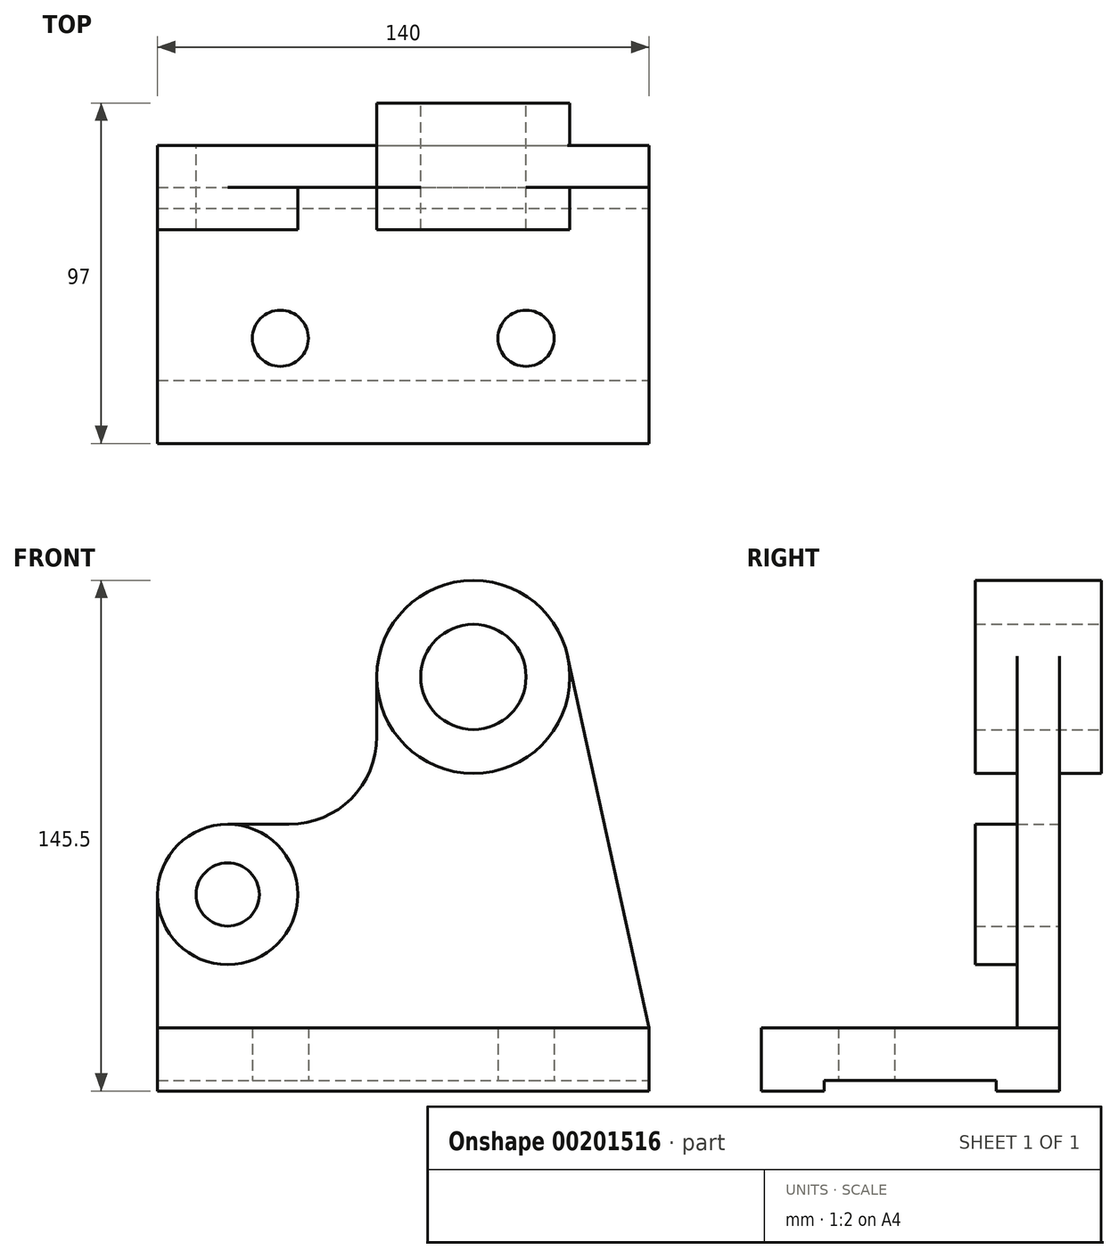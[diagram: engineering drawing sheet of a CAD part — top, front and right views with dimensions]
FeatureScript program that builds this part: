
annotation { "Feature Type Name" : "Feature", "Feature Type Description" : "" }
export const myFeature = defineFeature(function(context is Context, id is Id, definition is map)
    precondition{}
    {
        {
            var Q0;
            Q0=qCreatedBy(makeId("Front.planeOp"),FACE);
            var sketch = newSketch(context, id + "F0", { "sketchPlane" : qUnion([Q0])});
            skLineSegment(sketch, "E0.bottom", {"start": v(-70, 0) * mm, "end": v(70, 0) * mm});
            skLineSegment(sketch, "E0.top", {"start": v(-70, -18) * mm, "end": v(70, -18) * mm});
            skLineSegment(sketch, "E0.left", {"start": v(-70, 0) * mm, "end": v(-70, -18) * mm});
            skLineSegment(sketch, "E0.right", {"start": v(70, 0) * mm, "end": v(70, -18) * mm});
            skLineSegment(sketch, "E1", {"start": v(-70, 0) * mm, "end": v(-70, 38) * mm});
            skLineSegment(sketch, "E2", {"start": v(-50, 58) * mm, "end": v(-32.5, 58) * mm});
            skLineSegment(sketch, "E3", {"start": v(70, 0) * mm, "end": v(46.87, 105.87) * mm});
            skCircle(sketch, "E4", {"center": v(-50, 38) * mm, "radius": 20 * mm});
            skCircle(sketch, "E5", {"center": v(20, 100) * mm, "radius": 27.5 * mm});
            skArc(sketch, "E6", {"start": v(-32.5, 58) * mm, "mid": v(-14.82, 65.32) * mm, "end": v(-7.5, 83) * mm});
            skLineSegment(sketch, "E7", {"start": v(-7.5, 100) * mm, "end": v(-7.5, 83) * mm});
            skCircle(sketch, "E8", {"center": v(-50, 38) * mm, "radius": 9 * mm});
            skCircle(sketch, "E9", {"center": v(20, 100) * mm, "radius": 15 * mm});
            skSolve(sketch);
        }
        {
            var Q0;
            Q0=makeQuery(id+"F0.imprint","IMPRINT",FACE,{"disambiguationData":[TD([[makeQuery(id+"F0.imprint","IMPRINT",EDGE,{"derivedFrom":sQuery(id+"F0.wireOp",EDGE,"E0.bottom")}),-1.0]])]});
            extrude(context, id + "F1", {"entities" : qUnion([Q0]), "depth" : 85 * mm});
        }
        {
            var Q0;
            Q0=makeQuery(id+"F0.imprint","IMPRINT",FACE,{"disambiguationData":[TD([[makeQuery(id+"F0.imprint","IMPRINT",EDGE,{"derivedFrom":sQuery(id+"F0.wireOp",EDGE,"E0.bottom")}),1.0]])]});
            var Q1;
            Q1=makeQuery(id+"F0.imprint","IMPRINT",FACE,{"disambiguationData":[TD([[makeQuery(id+"F0.imprint","IMPRINT",EDGE,{"derivedFrom":sQuery(id+"F0.wireOp",EDGE,"E8")}),-1.0]])]});
            var Q2;
            Q2=makeQuery(id+"F0.imprint","IMPRINT",FACE,{"disambiguationData":[TD([[makeQuery(id+"F0.imprint","IMPRINT",EDGE,{"derivedFrom":sQuery(id+"F0.wireOp",EDGE,"E9")}),-1.0]])]});
            extrude(context, id + "F2", {"entities" : qUnion([Q0, Q1, Q2]), "operationType" : NewBodyOperationType.ADD, "depth" : 12 * mm});
        }
        {
            var Q0;
            Q0=makeQuery(id+"F0.imprint","IMPRINT",FACE,{"disambiguationData":[TD([[makeQuery(id+"F0.imprint","IMPRINT",EDGE,{"derivedFrom":sQuery(id+"F0.wireOp",EDGE,"E8")}),-1.0]])]});
            extrude(context, id + "F3", {"entities" : qUnion([Q0]), "operationType" : NewBodyOperationType.ADD, "depth" : 24 * mm});
        }
        {
            var Q0;
            Q0=makeQuery(id+"F0.imprint","IMPRINT",FACE,{"disambiguationData":[TD([[makeQuery(id+"F0.imprint","IMPRINT",EDGE,{"derivedFrom":sQuery(id+"F0.wireOp",EDGE,"E9")}),-1.0]])]});
            extrude(context, id + "F4", {"entities" : qUnion([Q0]), "operationType" : NewBodyOperationType.ADD, "depth" : 24 * mm, "hasSecondDirection" : true, "secondDirectionOppositeDirection" : true, "secondDirectionDepth" : (18 - 6) * mm});
        }
        {
            var Q0;
            Q0=makeQuery(id+"F1.opExtrude","SWEPT_FACE",FACE,{"disambiguationData":[OSD([sQuery(id+"F0.wireOp",EDGE,"E0.top")])]});
            var sketch = newSketch(context, id + "F5", { "sketchPlane" : qUnion([Q0])});
            skLineSegment(sketch, "E10.bottom", {"start": v(-70, 67) * mm, "end": v(70, 67) * mm});
            skLineSegment(sketch, "E10.top", {"start": v(-70, 18) * mm, "end": v(70, 18) * mm});
            skLineSegment(sketch, "E10.left", {"start": v(-70, 67) * mm, "end": v(-70, 18) * mm});
            skLineSegment(sketch, "E10.right", {"start": v(70, 67) * mm, "end": v(70, 18) * mm});
            skCircle(sketch, "E11", {"center": v(-35, 55) * mm, "radius": 8 * mm});
            skCircle(sketch, "E12", {"center": v(35, 55) * mm, "radius": 8 * mm});
            skSolve(sketch);
        }
        {
            var Q0;
            Q0=makeQuery(id+"F5.imprint","IMPRINT",FACE,{"disambiguationData":[TD([[makeQuery(id+"F5.imprint","IMPRINT",EDGE,{"derivedFrom":sQuery(id+"F5.wireOp",EDGE,"E10.bottom")}),-1.0]])]});
            extrude(context, id + "F6", {"entities" : qUnion([Q0]), "operationType" : NewBodyOperationType.REMOVE, "oppositeDirection" : true, "depth" : 3 * mm});
        }
        {
            var Q0;
            Q0=makeQuery(id+"F6.boolean.opBoolean","SPLIT",FACE,{"disambiguationData":[TD([makeQuery(id+"F6.opExtrude","SWEPT_FACE",FACE,{"disambiguationData":[OSD([sQuery(id+"F5.wireOp",EDGE,"E11")])]})])],"derivedFrom":makeQuery(id+"F1.opExtrude","SWEPT_FACE",FACE,{"disambiguationData":[OSD([sQuery(id+"F0.wireOp",EDGE,"E0.top")])]})});
            var Q1;
            Q1=makeQuery(id+"F6.boolean.opBoolean","SPLIT",FACE,{"disambiguationData":[TD([makeQuery(id+"F6.opExtrude","SWEPT_FACE",FACE,{"disambiguationData":[OSD([sQuery(id+"F5.wireOp",EDGE,"E12")])]})])],"derivedFrom":makeQuery(id+"F1.opExtrude","SWEPT_FACE",FACE,{"disambiguationData":[OSD([sQuery(id+"F0.wireOp",EDGE,"E0.top")])]})});
            extrude(context, id + "F7", {"entities" : qUnion([Q0, Q1]), "operationType" : NewBodyOperationType.REMOVE, "oppositeDirection" : true, "depth" : 25 * mm});
        }
    });
